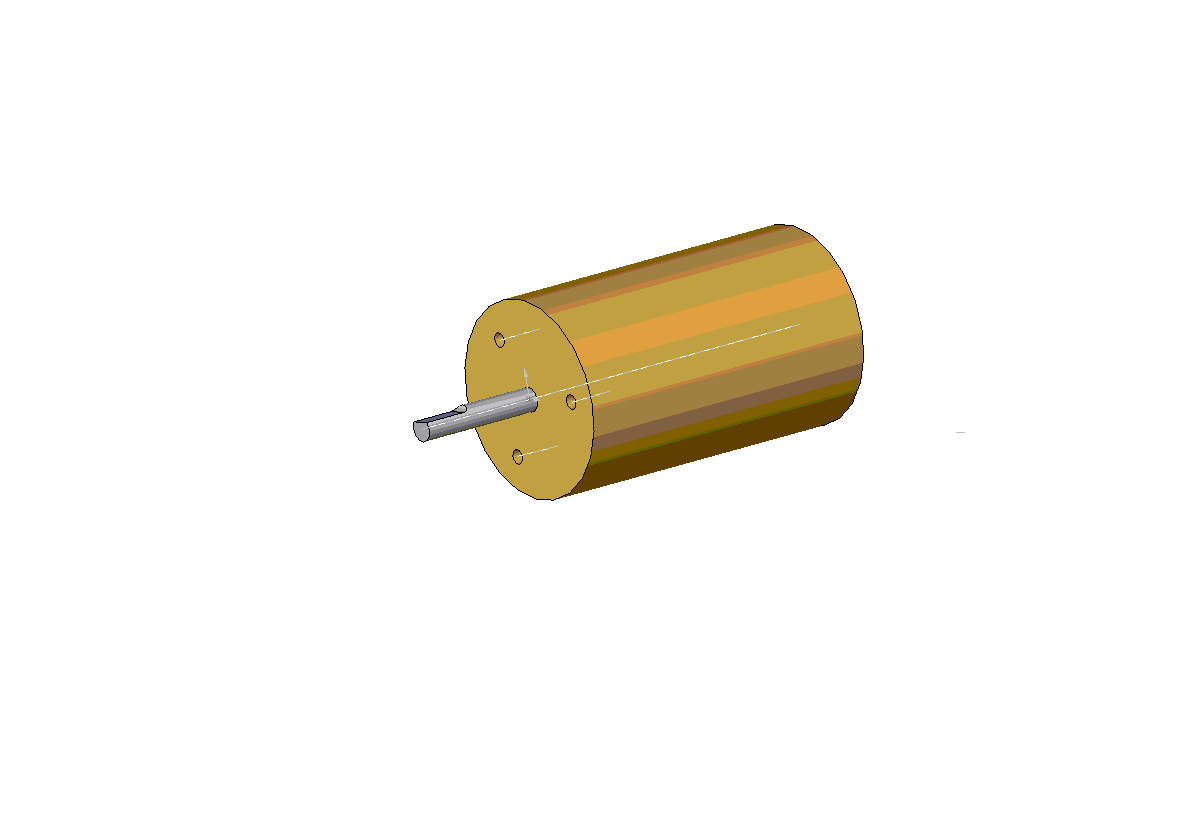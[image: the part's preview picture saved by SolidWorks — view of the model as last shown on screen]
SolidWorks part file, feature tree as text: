
SOLIDWORKS PART (.sldprt)
format: sldprt  version: not decoded by parser v0  size: 171,008 bytes
history: native  units: mm
features: sketch x5, extrude x2, cut_extrude x1, hole x1, pattern_circular x1 (+8 scaffold rows collapsed)
feature tree (18):
  scaffold x8  (default folders/planes/origin — collapsed)
  sketch  "Sketch1"  dims[body_diameter=38.1mm]
  extrude  "body"  Depth=63.5mm body_length=63.5mm
  sketch  "Sketch2"  dims[shaft_diameter=4.7625mm]
  extrude  "shaft"  Depth=25.4mm shaft_length=25.4mm
  sketch  "Sketch3"  dims[D2=1.5875mm D1=10.16mm D3=1.016mm]
  cut_extrude  "shaft-flat"  [1 undecoded]
  hole  "mounting_hole"  Diameter=2.2606mm Depth=8.8646mm
  sketch  "Sketch5"  dims[bolt_circle_radius=12.7mm]
  sketch  "Sketch4"  dims[hole-wizard template sketch: 29 standard entries collapsed; hole parameters kept: c8.Tap Drill Depth=8.8646mm c8.Thread Dia.=2.8448mm c8.Thread Depth=5.6896mm c8.D5=~14.816244mm c8.Drill Angle=118.0deg]
  pattern_circular  "CirPattern1"  Count=3 Angle=360deg
decode coverage: 9 of 10 modeling features carry decoded parameters
note: ~ marks probable driven/reference dimensions
note: 1 parameter value undecoded
note: suppression state not decoded; provenance and decode notes live in map.json
